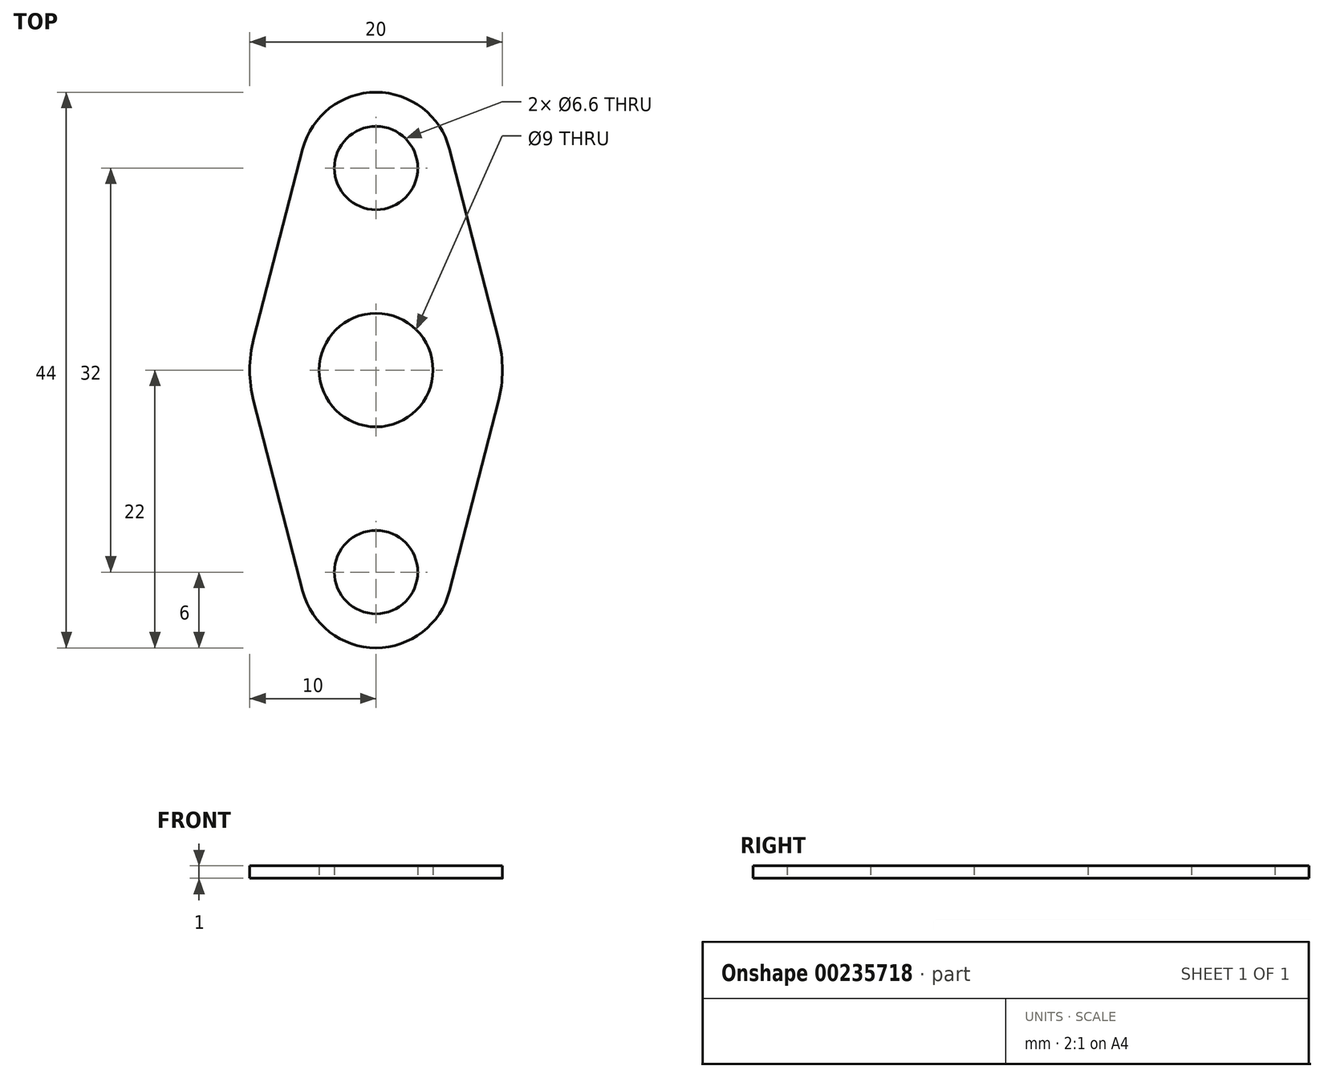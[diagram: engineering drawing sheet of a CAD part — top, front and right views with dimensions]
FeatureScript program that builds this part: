
annotation { "Feature Type Name" : "Feature", "Feature Type Description" : "" }
export const myFeature = defineFeature(function(context is Context, id is Id, definition is map)
    precondition{}
    {
        {
            var Q0;
            Q0=qCreatedBy(makeId("Top.planeOp"),FACE);
            var sketch = newSketch(context, id + "F0", { "sketchPlane" : qUnion([Q0])});
            skCircle(sketch, "E0", {"center": v(0, 0) * mm, "radius": 10 * mm});
            skCircle(sketch, "E1", {"center": v(0, 0) * mm, "radius": 4.5 * mm});
            skLineSegment(sketch, "E2", {"start": v(0, 0) * mm, "end": v(0, 16) * mm, "construction": true});
            skLineSegment(sketch, "E3", {"start": v(0, 0) * mm, "end": v(0, -16) * mm, "construction": true});
            skCircle(sketch, "E4", {"center": v(0, 16) * mm, "radius": 6 * mm});
            skCircle(sketch, "E5", {"center": v(0, -16) * mm, "radius": 6 * mm});
            skCircle(sketch, "E6", {"center": v(0, 16) * mm, "radius": 3.3 * mm});
            skCircle(sketch, "E7", {"center": v(0, -16) * mm, "radius": 3.3 * mm});
            skLineSegment(sketch, "E8", {"start": v(-6, 16) * mm, "end": v(6, 16) * mm, "construction": true});
            skLineSegment(sketch, "E9", {"start": v(-6, -16) * mm, "end": v(6, -16) * mm, "construction": true});
            skLineSegment(sketch, "E10", {"start": v(-10, 0) * mm, "end": v(10, 0) * mm, "construction": true});
            skLineSegment(sketch, "E11", {"start": v(-9.68, 2.5) * mm, "end": v(-5.8, 17.5) * mm});
            skLineSegment(sketch, "E12", {"start": v(9.68, 2.5) * mm, "end": v(5.8, 17.5) * mm});
            skLineSegment(sketch, "E13", {"start": v(9.68, -2.5) * mm, "end": v(5.8, -17.5) * mm});
            skLineSegment(sketch, "E14", {"start": v(-9.68, -2.5) * mm, "end": v(-5.8, -17.5) * mm});
            skSolve(sketch);
        }
        {
            var Q0;
            Q0=makeQuery(id+"F0.imprint","IMPRINT",FACE,{"disambiguationData":[TD([[makeQuery(id+"F0.imprint","IMPRINT",EDGE,{"derivedFrom":sQuery(id+"F0.wireOp",EDGE,"E6")}),1.0]])]});
            var Q1;
            Q1=makeQuery(id+"F0.imprint","IMPRINT",FACE,{"disambiguationData":[TD([[makeQuery(id+"F0.imprint","IMPRINT",EDGE,{"derivedFrom":sQuery(id+"F0.wireOp",EDGE,"E1")}),1.0]])]});
            var Q2;
            Q2=makeQuery(id+"F0.imprint","IMPRINT",FACE,{"disambiguationData":[TD([[makeQuery(id+"F0.imprint","IMPRINT",EDGE,{"derivedFrom":sQuery(id+"F0.wireOp",EDGE,"E7")}),1.0]])]});
            var Q3;
            {var subQ0=sQuery(id+"F0.wireOp",EDGE,"E12");Q3=makeQuery(id+"F0.imprint","IMPRINT",FACE,{"disambiguationData":[TD([[makeQuery(id+"F0.imprint","IMPRINT",EDGE,{"derivedFrom":subQ0}),1.0]])]});}
            var Q4;
            {var subQ0=sQuery(id+"F0.wireOp",EDGE,"E11");Q4=makeQuery(id+"F0.imprint","IMPRINT",FACE,{"disambiguationData":[TD([[makeQuery(id+"F0.imprint","IMPRINT",EDGE,{"derivedFrom":subQ0}),-1.0]])]});}
            var Q5;
            {var subQ0=sQuery(id+"F0.wireOp",EDGE,"E13");Q5=makeQuery(id+"F0.imprint","IMPRINT",FACE,{"disambiguationData":[TD([[makeQuery(id+"F0.imprint","IMPRINT",EDGE,{"derivedFrom":subQ0}),-1.0]])]});}
            var Q6;
            {var subQ0=sQuery(id+"F0.wireOp",EDGE,"E14");Q6=makeQuery(id+"F0.imprint","IMPRINT",FACE,{"disambiguationData":[TD([[makeQuery(id+"F0.imprint","IMPRINT",EDGE,{"derivedFrom":subQ0}),1.0]])]});}
            var Q7;
            Q7=makeQuery(id+"F0.imprint","IMPRINT",FACE,{"disambiguationData":[TD([[makeQuery(id+"F0.imprint","IMPRINT",EDGE,{"derivedFrom":sQuery(id+"F0.wireOp",EDGE,"E7")}),-1.0]])]});
            var Q8;
            Q8=makeQuery(id+"F0.imprint","IMPRINT",FACE,{"disambiguationData":[TD([[makeQuery(id+"F0.imprint","IMPRINT",EDGE,{"derivedFrom":sQuery(id+"F0.wireOp",EDGE,"E6")}),-1.0]])]});
            var Q9;
            Q9=makeQuery(id+"F0.imprint","IMPRINT",FACE,{"disambiguationData":[TD([[makeQuery(id+"F0.imprint","IMPRINT",EDGE,{"derivedFrom":sQuery(id+"F0.wireOp",EDGE,"E1")}),-1.0]])]});
            extrude(context, id + "F1", {"entities" : qUnion([Q0, Q1, Q2, Q3, Q4, Q5, Q6, Q7, Q8, Q9]), "depth" : 1 * mm});
        }
        {
            var Q0;
            Q0=sQuery(id+"F0.wireOp",VERTEX,"E4.center");
            var Q1;
            Q1=makeQuery(id+"F1.opExtrude","SWEPT_BODY",BODY,{"disambiguationData":[OSD([sQuery(id+"F0.wireOp",EDGE,"E0"),sQuery(id+"F0.wireOp",EDGE,"E4"),sQuery(id+"F0.wireOp",EDGE,"E5"),sQuery(id+"F0.wireOp",EDGE,"E11"),sQuery(id+"F0.wireOp",EDGE,"E12"),sQuery(id+"F0.wireOp",EDGE,"E13"),sQuery(id+"F0.wireOp",EDGE,"E14")])]});
            hole(context, id + "F2", {"style" : HoleStyle.SIMPLE, "endStyle" : HoleEndStyle.THROUGH, "oppositeDirection" : true, "holeDiameter" : 6.6 * mm, "locations" : qUnion([Q0]), "scope" : qUnion([Q1]), "isTappedThrough" : true});
        }
        {
            var Q0;
            Q0=sQuery(id+"F0.wireOp",VERTEX,"E7.center");
            var Q1;
            Q1=makeQuery(id+"F1.opExtrude","SWEPT_BODY",BODY,{"disambiguationData":[OSD([sQuery(id+"F0.wireOp",EDGE,"E0"),sQuery(id+"F0.wireOp",EDGE,"E4"),sQuery(id+"F0.wireOp",EDGE,"E5"),sQuery(id+"F0.wireOp",EDGE,"E11"),sQuery(id+"F0.wireOp",EDGE,"E12"),sQuery(id+"F0.wireOp",EDGE,"E13"),sQuery(id+"F0.wireOp",EDGE,"E14")])]});
            hole(context, id + "F3", {"style" : HoleStyle.SIMPLE, "endStyle" : HoleEndStyle.THROUGH, "oppositeDirection" : true, "holeDiameter" : 6.6 * mm, "locations" : qUnion([Q0]), "scope" : qUnion([Q1]), "isTappedThrough" : true});
        }
        {
            var Q0;
            Q0=sQuery(id+"F0.wireOp",VERTEX,"E0.center");
            var Q1;
            Q1=makeQuery(id+"F1.opExtrude","SWEPT_BODY",BODY,{"disambiguationData":[OSD([sQuery(id+"F0.wireOp",EDGE,"E0"),sQuery(id+"F0.wireOp",EDGE,"E4"),sQuery(id+"F0.wireOp",EDGE,"E5"),sQuery(id+"F0.wireOp",EDGE,"E11"),sQuery(id+"F0.wireOp",EDGE,"E12"),sQuery(id+"F0.wireOp",EDGE,"E13"),sQuery(id+"F0.wireOp",EDGE,"E14")])]});
            hole(context, id + "F4", {"style" : HoleStyle.SIMPLE, "endStyle" : HoleEndStyle.THROUGH, "oppositeDirection" : true, "holeDiameter" : 9 * mm, "locations" : qUnion([Q0]), "scope" : qUnion([Q1]), "isTappedThrough" : true});
        }
    });
